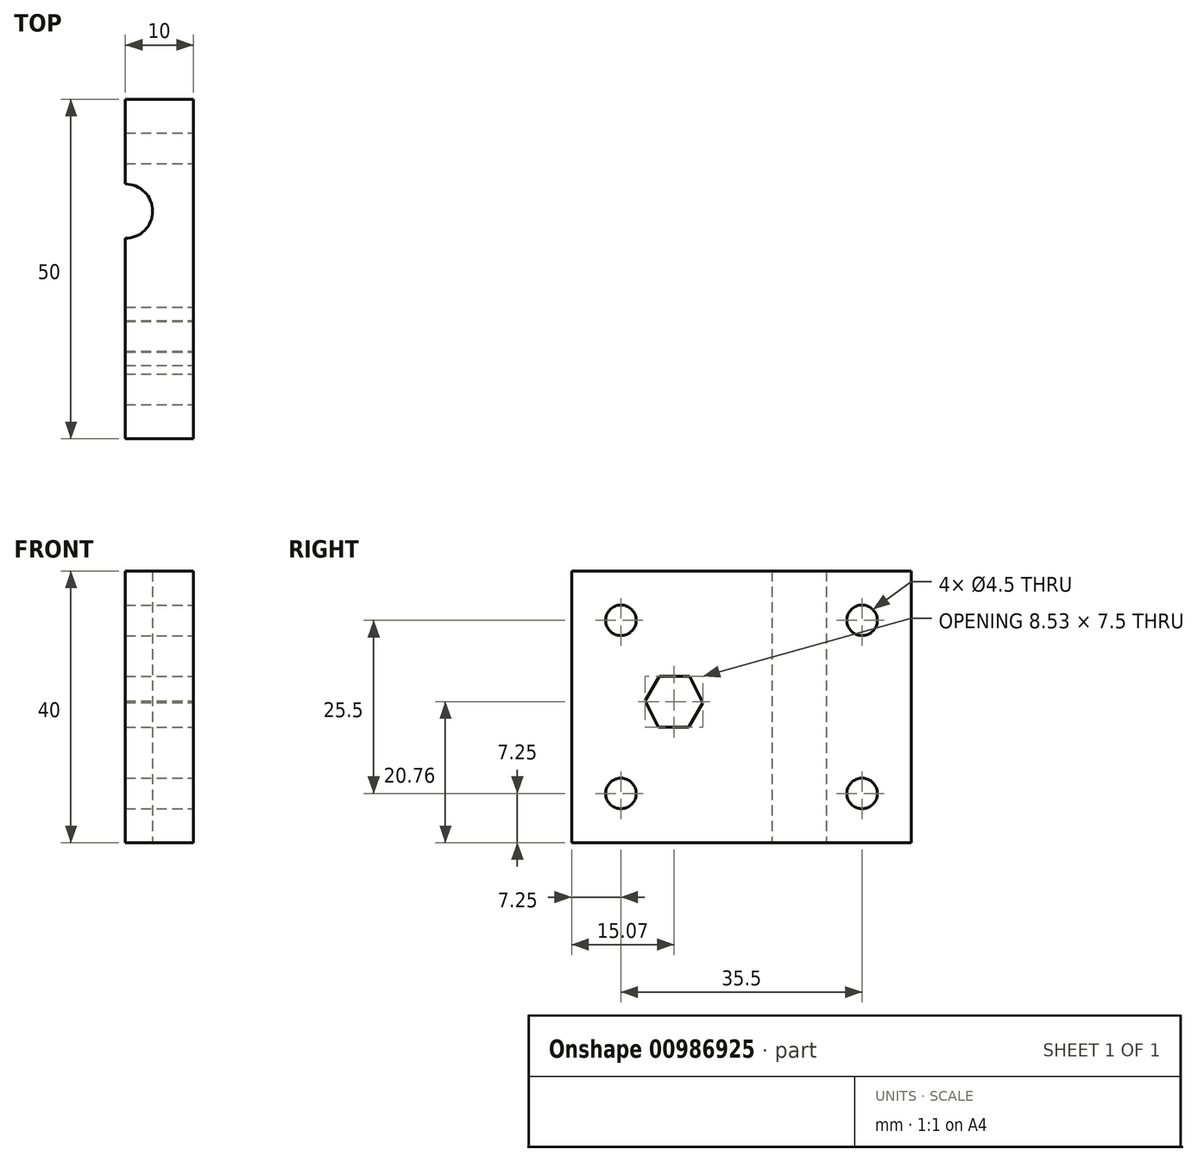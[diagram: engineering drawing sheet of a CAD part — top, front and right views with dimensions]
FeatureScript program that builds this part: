
annotation { "Feature Type Name" : "Feature", "Feature Type Description" : "" }
export const myFeature = defineFeature(function(context is Context, id is Id, definition is map)
    precondition{}
    {
        {
            var Q0;
            Q0=qCreatedBy(makeId("Top.planeOp"),FACE);
            var sketch = newSketch(context, id + "F0", { "sketchPlane" : qUnion([Q0])});
            skLineSegment(sketch, "E0.bottom", {"start": v(10, -25) * mm, "end": v(0, -25) * mm});
            skLineSegment(sketch, "E0.top", {"start": v(10, 25) * mm, "end": v(0, 25) * mm});
            skLineSegment(sketch, "E0.left", {"start": v(10, -25) * mm, "end": v(10, 25) * mm});
            skPoint(sketch, "E0.middle", {"position": v(0, 0) * mm});
            skArc(sketch, "E1", {"start": v(0, 4.5) * mm, "mid": v(4, 8.5) * mm, "end": v(0, 12.5) * mm});
            skPoint(sketch, "E1.centerSnap0", {"position": v(0, 25) * mm});
            skLineSegment(sketch, "E2", {"start": v(0, 25) * mm, "end": v(0, -25) * mm});
            skSolve(sketch);
        }
        {
            var Q0;
            {var subQ2=sQuery(id+"F0.wireOp",EDGE,"E0.bottom");Q0=makeQuery(id+"F0.imprint","IMPRINT",FACE,{"disambiguationData":[TD([[makeQuery(id+"F0.imprint","IMPRINT",EDGE,{"derivedFrom":subQ2}),-1.0]])]});}
            extrude(context, id + "F1", {"entities" : qUnion([Q0]), "depth" : 40 * mm, "offsetDistance" : 25 * mm});
        }
        {
            var Q0;
            Q0=makeQuery(id+"F1.opExtrude","SWEPT_FACE",FACE,{"disambiguationData":[OSD([sQuery(id+"F0.wireOp",EDGE,"E0.left")])]});
            var sketch = newSketch(context, id + "F2", { "sketchPlane" : qUnion([Q0])});
            skCircle(sketch, "E3", {"center": v(-17.75, 32.75) * mm, "radius": 2.25 * mm});
            skCircle(sketch, "E4", {"center": v(17.75, 32.75) * mm, "radius": 2.25 * mm});
            skCircle(sketch, "E5", {"center": v(17.75, 7.25) * mm, "radius": 2.25 * mm});
            skCircle(sketch, "E6", {"center": v(-17.75, 7.25) * mm, "radius": 2.25 * mm});
            skCircle(sketch, "E7.cCircle", {"center": v(-9.87, 20.64) * mm, "radius": 3.75 * mm, "construction": true});
            skLineSegment(sketch, "E7.0", {"start": v(-7.63, 24.51) * mm, "end": v(-5.67, 20.65) * mm});
            skLineSegment(sketch, "E7.1", {"start": v(-5.67, 20.65) * mm, "end": v(-7.76, 17.01) * mm});
            skLineSegment(sketch, "E7.2", {"start": v(-7.76, 17.01) * mm, "end": v(-12.23, 17.01) * mm});
            skLineSegment(sketch, "E7.3", {"start": v(-12.23, 17.01) * mm, "end": v(-14.2, 20.87) * mm});
            skLineSegment(sketch, "E7.4", {"start": v(-14.2, 20.87) * mm, "end": v(-12.1, 24.51) * mm});
            skLineSegment(sketch, "E7.5", {"start": v(-12.1, 24.51) * mm, "end": v(-7.63, 24.51) * mm});
            skPoint(sketch, "E7.0.midPoint", {"position": v(-6.65, 22.58) * mm});
            skSolve(sketch);
        }
        {
            var Q0;
            Q0=makeQuery(id+"F2.imprint","IMPRINT",FACE,{"disambiguationData":[TD([[makeQuery(id+"F2.imprint","IMPRINT",EDGE,{"derivedFrom":sQuery(id+"F2.wireOp",EDGE,"E3")}),1.0]])]});
            var Q1;
            Q1=makeQuery(id+"F2.imprint","IMPRINT",FACE,{"disambiguationData":[TD([[makeQuery(id+"F2.imprint","IMPRINT",EDGE,{"derivedFrom":sQuery(id+"F2.wireOp",EDGE,"E4")}),1.0]])]});
            var Q2;
            Q2=makeQuery(id+"F2.imprint","IMPRINT",FACE,{"disambiguationData":[TD([[makeQuery(id+"F2.imprint","IMPRINT",EDGE,{"derivedFrom":sQuery(id+"F2.wireOp",EDGE,"E5")}),1.0]])]});
            var Q3;
            Q3=makeQuery(id+"F2.imprint","IMPRINT",FACE,{"disambiguationData":[TD([[makeQuery(id+"F2.imprint","IMPRINT",EDGE,{"derivedFrom":sQuery(id+"F2.wireOp",EDGE,"E6")}),1.0]])]});
            var Q4;
            Q4=makeQuery(id+"F2.imprint","IMPRINT",FACE,{"disambiguationData":[TD([[makeQuery(id+"F2.imprint","IMPRINT",EDGE,{"derivedFrom":sQuery(id+"F2.wireOp",EDGE,"E7.0")}),-1.0]])]});
            extrude(context, id + "F3", {"entities" : qUnion([Q0, Q1, Q2, Q3, Q4]), "operationType" : NewBodyOperationType.REMOVE, "endBound" : BoundingType.THROUGH_ALL, "oppositeDirection" : true, "depth" : 25 * mm, "offsetDistance" : 25 * mm});
        }
    });
